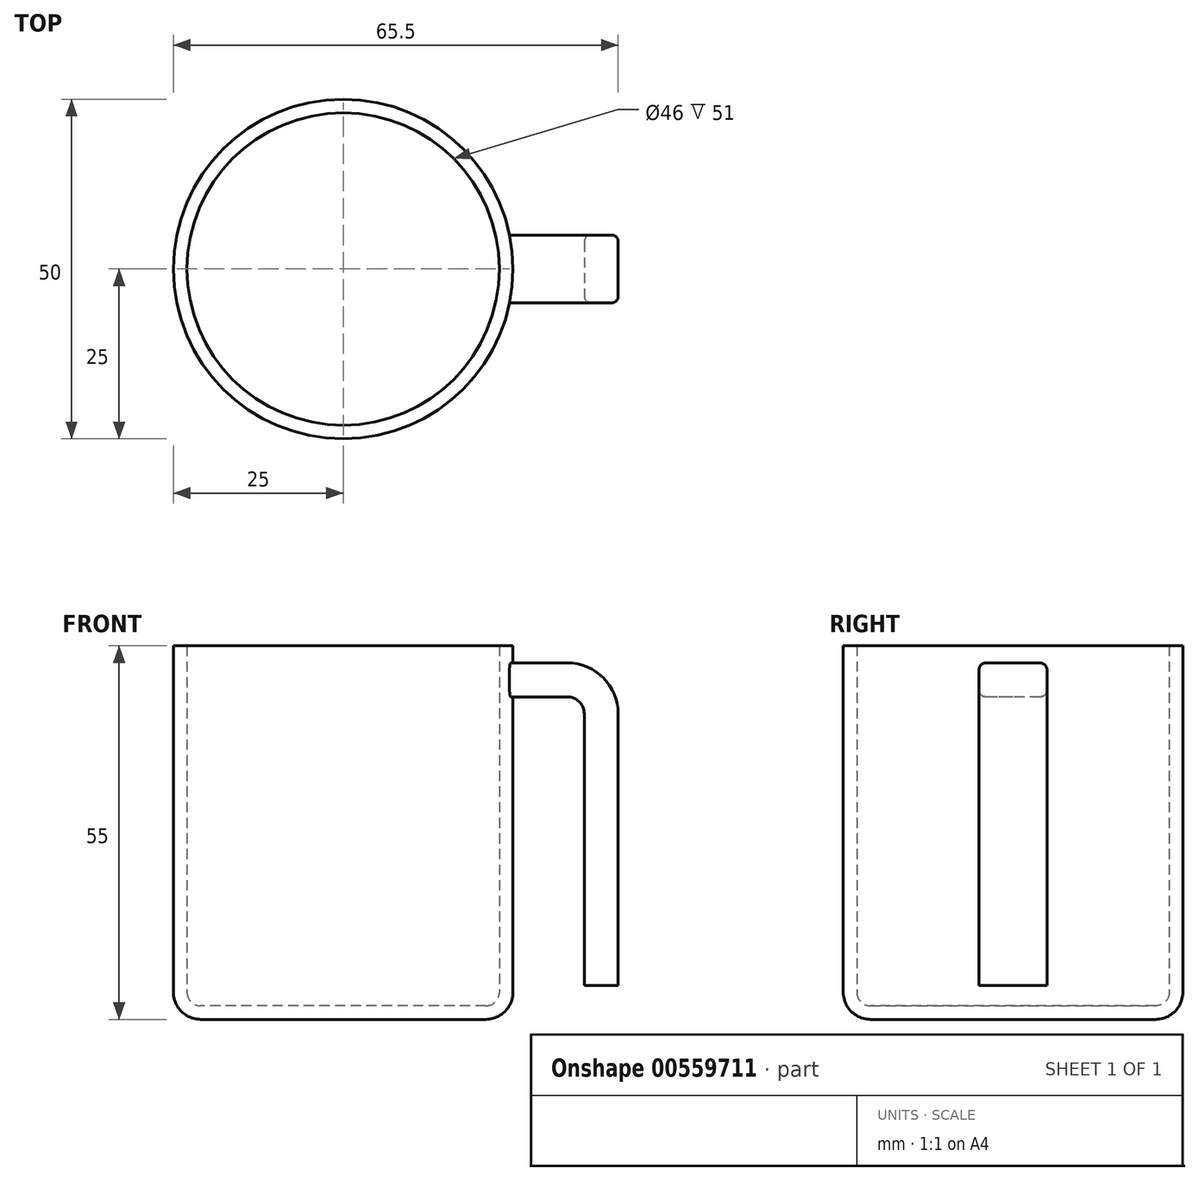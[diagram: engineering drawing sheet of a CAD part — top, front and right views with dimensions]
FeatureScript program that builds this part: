
annotation { "Feature Type Name" : "Feature", "Feature Type Description" : "" }
export const myFeature = defineFeature(function(context is Context, id is Id, definition is map)
    precondition{}
    {
        {
            var Q0;
            Q0=qCreatedBy(makeId("Top.planeOp"),FACE);
            var sketch = newSketch(context, id + "F0", { "sketchPlane" : qUnion([Q0])});
            skCircle(sketch, "E0", {"center": v(0, 0) * mm, "radius": 25 * mm});
            skSolve(sketch);
        }
        {
            var Q0;
            Q0=makeQuery(id+"F0.imprint","IMPRINT",FACE,{"disambiguationData":[TD([[makeQuery(id+"F0.imprint","IMPRINT",EDGE,{"derivedFrom":sQuery(id+"F0.wireOp",EDGE,"E0")}),1.0]])]});
            extrude(context, id + "F1", {"entities" : qUnion([Q0]), "depth" : 55 * mm, "offsetDistance" : 25 * mm});
        }
        {
            var Q0;
            Q0=makeQuery(id+"F1.opExtrude","CAP_EDGE",EDGE,{"disambiguationData":[OSD([sQuery(id+"F0.wireOp",EDGE,"E0")])],"isStart":true});
            fillet(context, id + "F2", {"entities" : qUnion([Q0]), "radius" : 4 * mm, "tangentPropagation" : true, "allowEdgeOverflow" : false});
        }
        {
            var Q0;
            Q0=makeQuery(id+"F1.opExtrude","CAP_FACE",FACE,{"disambiguationData":[OSD([sQuery(id+"F0.wireOp",EDGE,"E0")])],"isStart":false});
            shell(context, id + "F3", {"entities" : qUnion([Q0]), "thickness" : 2 * mm});
        }
        {
            var Q0;
            Q0=qCreatedBy(makeId("Front.planeOp"),FACE);
            var sketch = newSketch(context, id + "F4", { "sketchPlane" : qUnion([Q0])});
            skLineSegment(sketch, "E1", {"start": v(0, 50) * mm, "end": v(33, 50) * mm});
            skLineSegment(sketch, "E2", {"start": v(38, 45) * mm, "end": v(38, 5) * mm});
            skPoint(sketch, "E3.visualSharp", {"position": v(38, 50) * mm});
            skArc(sketch, "E3.filletArc", {"start": v(38, 45) * mm, "mid": v(36.54, 48.54) * mm, "end": v(33, 50) * mm});
            skSolve(sketch);
        }
        {
            var Q0;
            Q0=qCreatedBy(makeId("Right.planeOp"),FACE);
            var sketch = newSketch(context, id + "F5", { "sketchPlane" : qUnion([Q0])});
            skLineSegment(sketch, "E4.bottom", {"start": v(5, 47.5) * mm, "end": v(-5, 47.5) * mm});
            skLineSegment(sketch, "E4.top", {"start": v(5, 52.5) * mm, "end": v(-5, 52.5) * mm});
            skLineSegment(sketch, "E4.left", {"start": v(5, 47.5) * mm, "end": v(5, 52.5) * mm});
            skLineSegment(sketch, "E4.right", {"start": v(-5, 47.5) * mm, "end": v(-5, 52.5) * mm});
            skPoint(sketch, "E4.middle", {"position": v(0, 50) * mm});
            skSolve(sketch);
        }
        {
            var Q0;
            Q0=makeQuery(id+"F5.imprint","IMPRINT",FACE,{"disambiguationData":[TD([[makeQuery(id+"F5.imprint","IMPRINT",EDGE,{"derivedFrom":sQuery(id+"F5.wireOp",EDGE,"E4.bottom")}),-1.0]])]});
            var Q1;
            Q1=sQuery(id+"F4.wireOp",EDGE,"E1");
            var Q2;
            Q2=sQuery(id+"F4.wireOp",EDGE,"E3.filletArc");
            var Q3;
            Q3=sQuery(id+"F4.wireOp",EDGE,"E2");
            sweep(context, id + "F6", {"operationType" : NewBodyOperationType.ADD, "profiles" : qUnion([Q0]), "path" : qUnion([Q1, Q2, Q3])});
        }
        {
            var Q0;
            Q0=makeQuery(id+"F6.opSweep","CAP_FACE",FACE,{"disambiguationData":[OSD([sQuery(id+"F4.wireOp",VERTEX,"E1.start"),sQuery(id+"F5.wireOp",EDGE,"E4.bottom"),sQuery(id+"F5.wireOp",EDGE,"E4.top"),sQuery(id+"F5.wireOp",EDGE,"E4.left"),sQuery(id+"F5.wireOp",EDGE,"E4.right")])],"isStart":true});
            var Q1;
            {var subQ0=sQuery(id+"F0.wireOp",EDGE,"E0");Q1=makeQuery(id+"F3.opShell","OFFSET_FACE",FACE,{"disambiguationData":[OSD([subQ0]),TDD([makeQuery(id+"F1.opExtrude","SWEPT_FACE",FACE,{"disambiguationData":[OSD([subQ0])]})])]});}
            extrude(context, id + "F7", {"entities" : qUnion([Q0]), "operationType" : NewBodyOperationType.REMOVE, "endBound" : BoundingType.UP_TO_SURFACE, "oppositeDirection" : true, "depth" : 25 * mm, "endBoundEntityFace" : qUnion([Q1]), "offsetDistance" : 25 * mm});
        }
        {
            var Q0;
            Q0=makeQuery(id+"F6.opSweep","SWEPT_EDGE",EDGE,{"disambiguationData":[OSD([sQuery(id+"F4.wireOp",EDGE,"E2"),sQuery(id+"F5.wireOp",EDGE,"E4.top"),sQuery(id+"F5.wireOp",EDGE,"E4.right")])]});
            var Q1;
            Q1=makeQuery(id+"F6.opSweep","SWEPT_EDGE",EDGE,{"disambiguationData":[OSD([sQuery(id+"F4.wireOp",EDGE,"E2"),sQuery(id+"F5.wireOp",EDGE,"E4.bottom"),sQuery(id+"F5.wireOp",EDGE,"E4.right")])]});
            var Q2;
            Q2=makeQuery(id+"F6.opSweep","SWEPT_EDGE",EDGE,{"disambiguationData":[OSD([sQuery(id+"F4.wireOp",EDGE,"E2"),sQuery(id+"F5.wireOp",EDGE,"E4.bottom"),sQuery(id+"F5.wireOp",EDGE,"E4.left")])]});
            var Q3;
            Q3=makeQuery(id+"F6.opSweep","SWEPT_EDGE",EDGE,{"disambiguationData":[OSD([sQuery(id+"F4.wireOp",EDGE,"E2"),sQuery(id+"F5.wireOp",EDGE,"E4.top"),sQuery(id+"F5.wireOp",EDGE,"E4.left")])]});
            fillet(context, id + "F8", {"entities" : qUnion([Q0, Q1, Q2, Q3]), "radius" : 1 * mm, "tangentPropagation" : true, "allowEdgeOverflow" : false});
        }
    });
